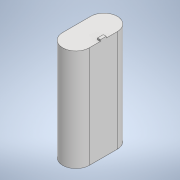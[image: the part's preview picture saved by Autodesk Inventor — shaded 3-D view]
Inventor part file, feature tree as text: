
AUTODESK INVENTOR PART (.ipt)
format: ipt  version: 2020.2 (Build 242310000, 310)  size: 112,128 bytes
history: native  units: in
note: dims shown in document units (in); Inventor stores cm internally (conversion verified against a paired STEP export)
features: extrude x2, sketch x2
ambient origin geometry x8: Origin, YZ Plane, XZ Plane, XY Plane, X Axis, Y Axis, Z Axis, Center Point
bodies: Solid1 (feature_tree)
feature tree (4):
  extrude  "Extrusion1"  Depth=0.7087in
  extrude  "Extrusion2"  Depth=0.3543in
  sketch  "Sketch1"  dims[d0=0.7087in d1=1.4567in]
  sketch  "Sketch2"  dims[d2=0.7283in d3=0.3543in d4=0.3543in d5=2.7165in d6=0.0in d7=0.0787in d8=0.1575in d9=0.0787in d10=0.0394in d11=0.0in]
